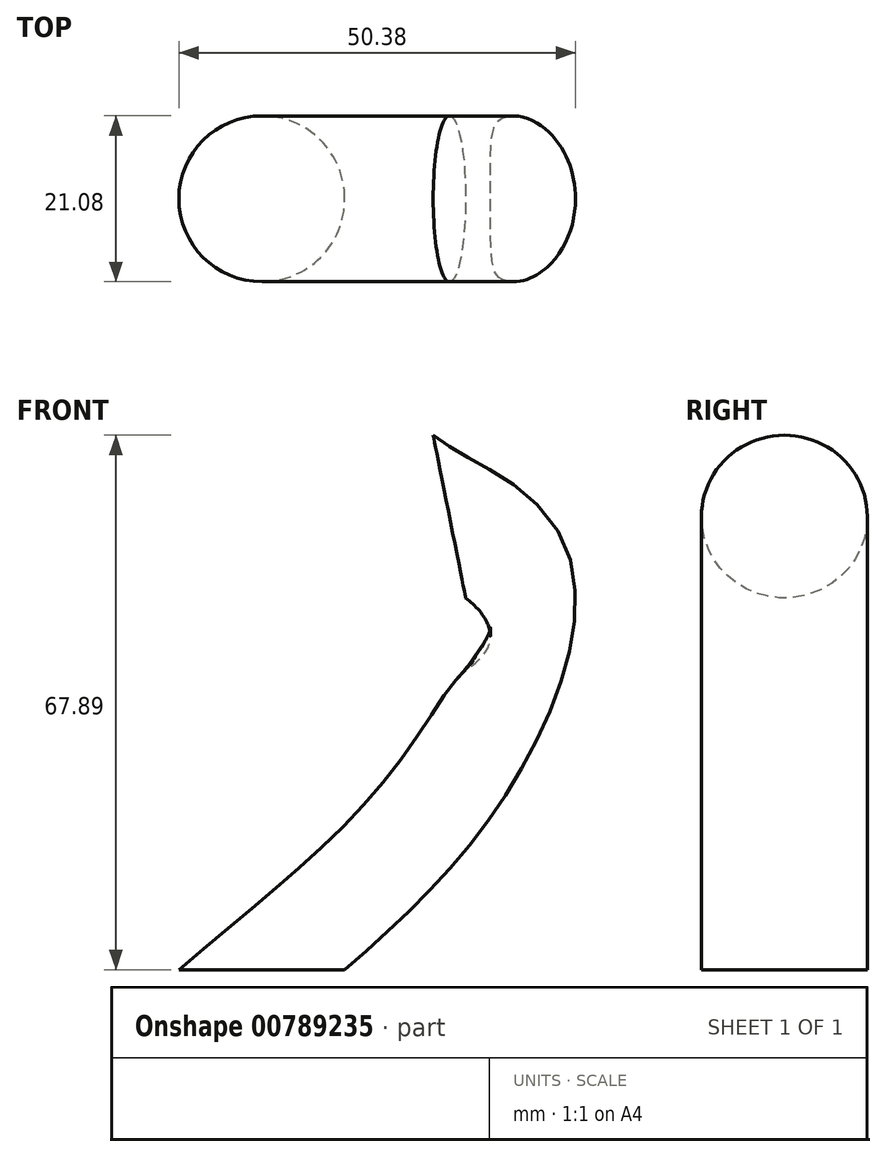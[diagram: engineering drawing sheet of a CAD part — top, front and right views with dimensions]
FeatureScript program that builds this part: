
annotation { "Feature Type Name" : "Feature", "Feature Type Description" : "" }
export const myFeature = defineFeature(function(context is Context, id is Id, definition is map)
    precondition{}
    {
        {
            var Q0;
            Q0=qCreatedBy(makeId("Front.planeOp"),FACE);
            var sketch = newSketch(context, id + "F0", { "sketchPlane" : qUnion([Q0])});
            skFitSpline(sketch, "E0", {"points": [v(0, 0) * mm, v(23.28, 23.74) * mm, v(31.71, 47.66) * mm, v(23.83, 57.56) * mm], "startDerivative": vector(63, 54.14) * mm, "endDerivative": vector(-42.47, 33.21) * mm});
            skSolve(sketch);
        }
        {
            var Q0;
            Q0=qCreatedBy(makeId("Top.planeOp"),FACE);
            var sketch = newSketch(context, id + "F1", { "sketchPlane" : qUnion([Q0])});
            skCircle(sketch, "E1", {"center": v(0, 0) * mm, "radius": 10.54 * mm});
            skSolve(sketch);
        }
        {
            var Q0;
            Q0=makeQuery(id+"F1.imprint","IMPRINT",FACE,{"disambiguationData":[TD([[makeQuery(id+"F1.imprint","IMPRINT",EDGE,{"derivedFrom":sQuery(id+"F1.wireOp",EDGE,"E1")}),1.0]])]});
            var Q1;
            Q1=sQuery(id+"F0.wireOp",EDGE,"E0");
            sweep(context, id + "F2", {"profiles" : qUnion([Q0]), "path" : qUnion([Q1])});
        }
    });
